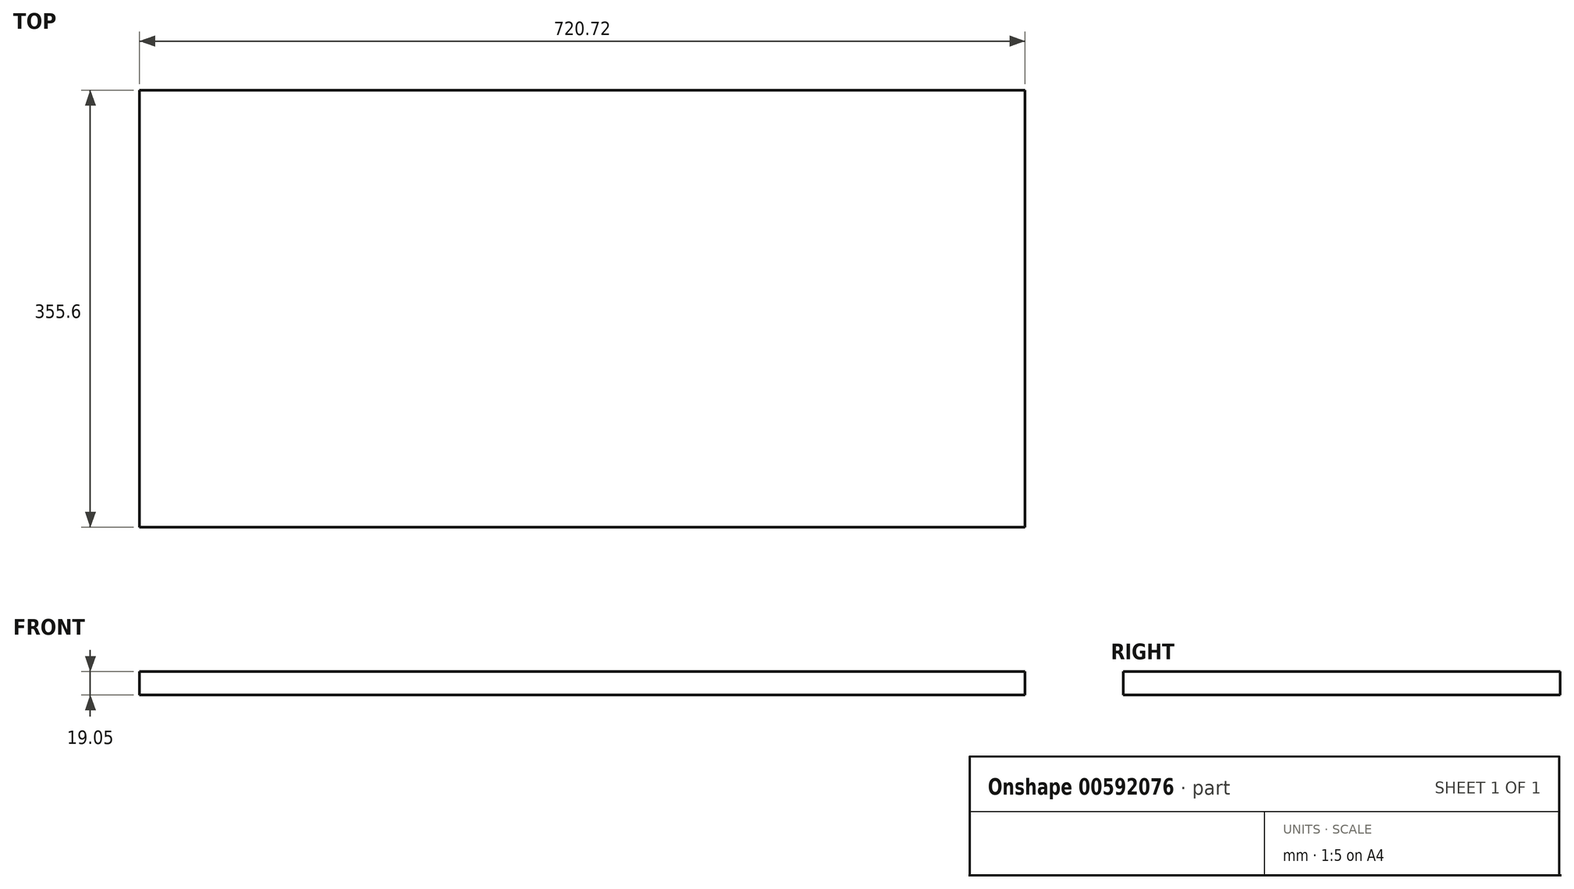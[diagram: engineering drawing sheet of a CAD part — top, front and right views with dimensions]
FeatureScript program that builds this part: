
annotation { "Feature Type Name" : "Feature", "Feature Type Description" : "" }
export const myFeature = defineFeature(function(context is Context, id is Id, definition is map)
    precondition{}
    {
        {
            var Q0;
            Q0=qCreatedBy(makeId("Top.planeOp"),FACE);
            var sketch = newSketch(context, id + "F0", { "sketchPlane" : qUnion([Q0])});
            skLineSegment(sketch, "E0.bottom", {"start": v(360.36, 177.8) * mm, "end": v(-360.36, 177.8) * mm});
            skLineSegment(sketch, "E0.top", {"start": v(360.36, -177.8) * mm, "end": v(-360.36, -177.8) * mm});
            skLineSegment(sketch, "E0.left", {"start": v(360.36, 177.8) * mm, "end": v(360.36, -177.8) * mm});
            skLineSegment(sketch, "E0.right", {"start": v(-360.36, 177.8) * mm, "end": v(-360.36, -177.8) * mm});
            skPoint(sketch, "E0.middle", {"position": v(0, 0) * mm});
            skSolve(sketch);
        }
        {
            var Q0;
            Q0=makeQuery(id+"F0.imprint","IMPRINT",FACE,{"disambiguationData":[TD([[makeQuery(id+"F0.imprint","IMPRINT",EDGE,{"derivedFrom":sQuery(id+"F0.wireOp",EDGE,"E0.bottom")}),1.0]])]});
            extrude(context, id + "F1", {"entities" : qUnion([Q0]), "depth" : 19.05 * mm, "offsetDistance" : 25.4 * mm});
        }
    });
